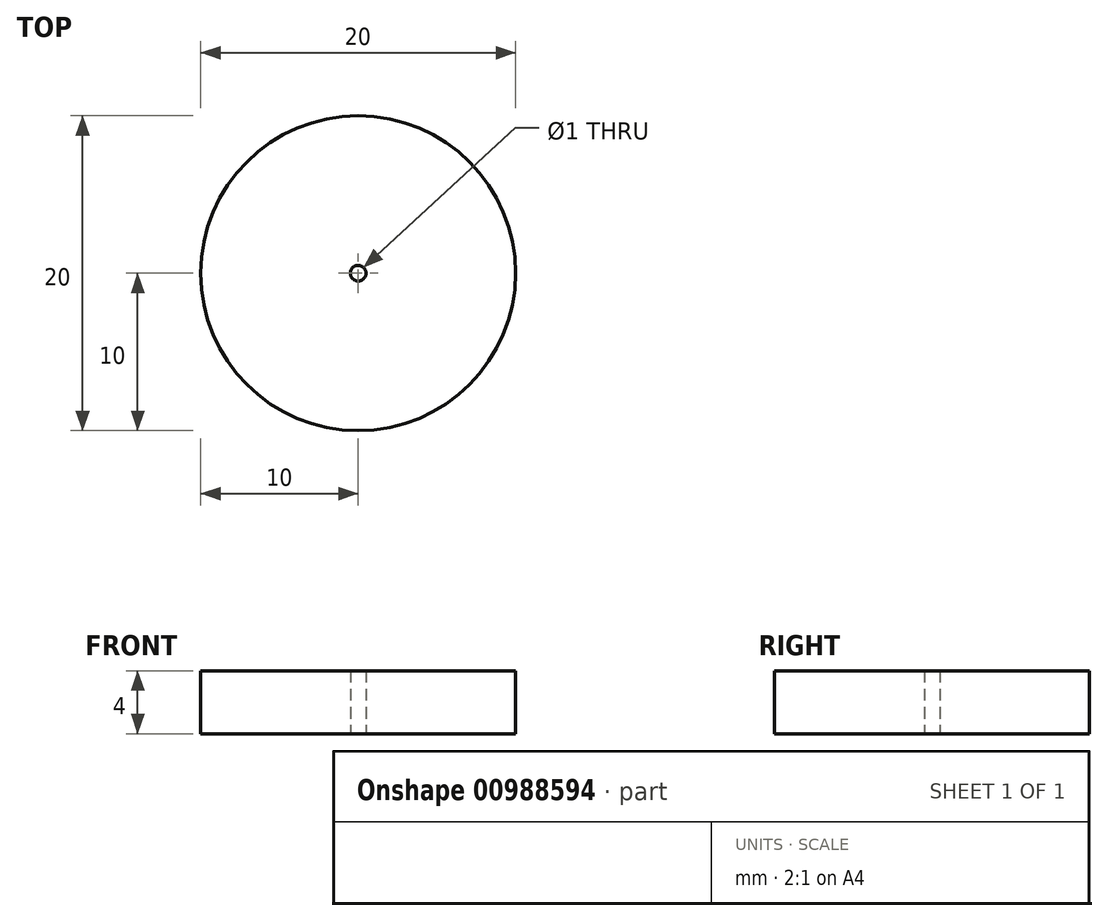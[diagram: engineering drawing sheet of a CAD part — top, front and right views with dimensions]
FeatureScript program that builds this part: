
annotation { "Feature Type Name" : "Feature", "Feature Type Description" : "" }
export const myFeature = defineFeature(function(context is Context, id is Id, definition is map)
    precondition{}
    {
        {
            var Q0;
            Q0=qCreatedBy(makeId("Top.planeOp"),FACE);
            var sketch = newSketch(context, id + "F0", { "sketchPlane" : qUnion([Q0])});
            skCircle(sketch, "E0", {"center": v(0, 0) * mm, "radius": 10 * mm});
            skCircle(sketch, "E1", {"center": v(0, 0) * mm, "radius": 0.5 * mm});
            skSolve(sketch);
        }
        {
            var Q0;
            Q0 = qSketchRegion(id + "F0", true);
            extrude(context, id + "F1", {"entities" : qUnion([Q0]), "depth" : 4 * mm, "offsetDistance" : 25 * mm});
        }
    });
